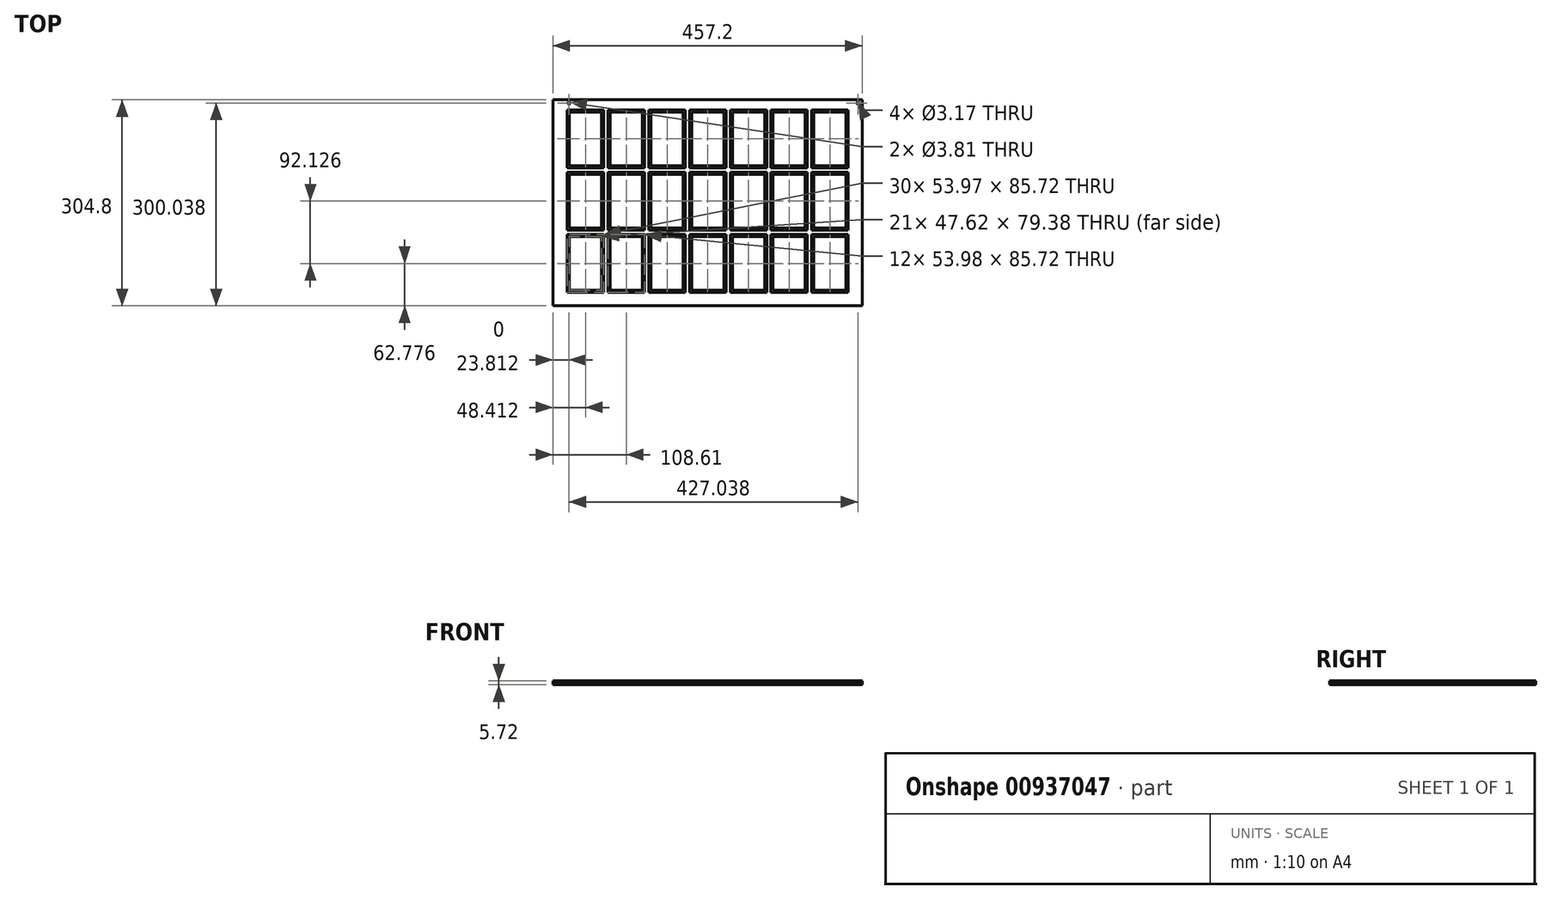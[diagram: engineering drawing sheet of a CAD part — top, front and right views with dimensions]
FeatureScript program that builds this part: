
annotation { "Feature Type Name" : "Feature", "Feature Type Description" : "" }
export const myFeature = defineFeature(function(context is Context, id is Id, definition is map)
    precondition{}
    {
        {
            var Q0;
            Q0=qCreatedBy(makeId("Top.planeOp"),FACE);
            var sketch = newSketch(context, id + "F0", { "sketchPlane" : qUnion([Q0])});
            skLineSegment(sketch, "E0.bottom", {"start": v(-228.6, 152.4) * mm, "end": v(228.6, 152.4) * mm});
            skLineSegment(sketch, "E0.top", {"start": v(-228.6, -152.4) * mm, "end": v(228.6, -152.4) * mm});
            skLineSegment(sketch, "E0.left", {"start": v(-228.6, 152.4) * mm, "end": v(-228.6, -152.4) * mm});
            skLineSegment(sketch, "E0.right", {"start": v(228.6, 152.4) * mm, "end": v(228.6, -152.4) * mm});
            skPoint(sketch, "E0.middle", {"position": v(0, 0) * mm});
            skCircle(sketch, "E1", {"center": v(-204.79, 147.64) * mm, "radius": 1.59 * mm});
            skCircle(sketch, "E2", {"center": v(222.25, 147.64) * mm, "radius": 1.59 * mm});
            skSolve(sketch);
        }
        {
            var Q0;
            Q0=makeQuery(id+"F0.imprint","IMPRINT",FACE,{"disambiguationData":[TD([[makeQuery(id+"F0.imprint","IMPRINT",EDGE,{"derivedFrom":sQuery(id+"F0.wireOp",EDGE,"E0.bottom")}),-1.0]])]});
            extrude(context, id + "F1", {"entities" : qUnion([Q0]), "depth" : 2.54 * mm, "offsetDistance" : 25.4 * mm});
        }
        {
            var Q0;
            Q0=makeQuery(id+"F1.opExtrude","CAP_FACE",FACE,{"disambiguationData":[OSD([sQuery(id+"F0.wireOp",EDGE,"E0.bottom"),sQuery(id+"F0.wireOp",EDGE,"E0.top"),sQuery(id+"F0.wireOp",EDGE,"E0.left"),sQuery(id+"F0.wireOp",EDGE,"E0.right"),sQuery(id+"F0.wireOp",EDGE,"E1"),sQuery(id+"F0.wireOp",EDGE,"E2")])],"isStart":false});
            var sketch = newSketch(context, id + "F2", { "sketchPlane" : qUnion([Q0])});
            skLineSegment(sketch, "E3.bottom", {"start": v(-207.18, -46.76) * mm, "end": v(-153.2, -46.76) * mm});
            skLineSegment(sketch, "E3.top", {"start": v(-207.18, -132.49) * mm, "end": v(-153.2, -132.49) * mm});
            skLineSegment(sketch, "E3.left", {"start": v(-207.18, -46.76) * mm, "end": v(-207.18, -132.49) * mm});
            skLineSegment(sketch, "E3.right", {"start": v(-153.2, -46.76) * mm, "end": v(-153.2, -132.49) * mm});
            skLineSegment(sketch, "E4.0.1.0", {"start": v(-207.18, 45.36) * mm, "end": v(-153.2, 45.36) * mm});
            skLineSegment(sketch, "E4.0.1.1", {"start": v(-207.18, 45.36) * mm, "end": v(-207.18, -40.36) * mm});
            skLineSegment(sketch, "E4.0.1.2", {"start": v(-207.18, -40.36) * mm, "end": v(-153.2, -40.36) * mm});
            skLineSegment(sketch, "E4.0.1.3", {"start": v(-153.2, 45.36) * mm, "end": v(-153.2, -40.36) * mm});
            skLineSegment(sketch, "E4.0.2.0", {"start": v(-207.18, 137.5) * mm, "end": v(-153.2, 137.5) * mm});
            skLineSegment(sketch, "E4.0.2.1", {"start": v(-207.18, 137.5) * mm, "end": v(-207.18, 51.77) * mm});
            skLineSegment(sketch, "E4.0.2.2", {"start": v(-207.18, 51.77) * mm, "end": v(-153.2, 51.77) * mm});
            skLineSegment(sketch, "E4.0.2.3", {"start": v(-153.2, 137.5) * mm, "end": v(-153.2, 51.77) * mm});
            skLineSegment(sketch, "E4.1.0.0", {"start": v(-146.98, -46.76) * mm, "end": v(-93, -46.76) * mm});
            skLineSegment(sketch, "E4.1.0.1", {"start": v(-146.98, -46.76) * mm, "end": v(-146.98, -132.49) * mm});
            skLineSegment(sketch, "E4.1.0.2", {"start": v(-146.98, -132.49) * mm, "end": v(-93, -132.49) * mm});
            skLineSegment(sketch, "E4.1.0.3", {"start": v(-93, -46.76) * mm, "end": v(-93, -132.49) * mm});
            skLineSegment(sketch, "E4.1.1.0", {"start": v(-146.98, 45.36) * mm, "end": v(-93, 45.36) * mm});
            skLineSegment(sketch, "E4.1.1.1", {"start": v(-146.98, 45.36) * mm, "end": v(-146.98, -40.36) * mm});
            skLineSegment(sketch, "E4.1.1.2", {"start": v(-146.98, -40.36) * mm, "end": v(-93, -40.36) * mm});
            skLineSegment(sketch, "E4.1.1.3", {"start": v(-93, 45.36) * mm, "end": v(-93, -40.36) * mm});
            skLineSegment(sketch, "E4.1.2.0", {"start": v(-146.98, 137.5) * mm, "end": v(-93, 137.5) * mm});
            skLineSegment(sketch, "E4.1.2.1", {"start": v(-146.98, 137.5) * mm, "end": v(-146.98, 51.77) * mm});
            skLineSegment(sketch, "E4.1.2.2", {"start": v(-146.98, 51.77) * mm, "end": v(-93, 51.77) * mm});
            skLineSegment(sketch, "E4.1.2.3", {"start": v(-93, 137.5) * mm, "end": v(-93, 51.77) * mm});
            skLineSegment(sketch, "E4.2.0.0", {"start": v(-86.78, -46.76) * mm, "end": v(-32.8, -46.76) * mm});
            skLineSegment(sketch, "E4.2.0.1", {"start": v(-86.78, -46.76) * mm, "end": v(-86.78, -132.49) * mm});
            skLineSegment(sketch, "E4.2.0.2", {"start": v(-86.78, -132.49) * mm, "end": v(-32.8, -132.49) * mm});
            skLineSegment(sketch, "E4.2.0.3", {"start": v(-32.8, -46.76) * mm, "end": v(-32.8, -132.49) * mm});
            skLineSegment(sketch, "E4.2.1.0", {"start": v(-86.78, 45.36) * mm, "end": v(-32.8, 45.36) * mm});
            skLineSegment(sketch, "E4.2.1.1", {"start": v(-86.78, 45.36) * mm, "end": v(-86.78, -40.36) * mm});
            skLineSegment(sketch, "E4.2.1.2", {"start": v(-86.78, -40.36) * mm, "end": v(-32.8, -40.36) * mm});
            skLineSegment(sketch, "E4.2.1.3", {"start": v(-32.8, 45.36) * mm, "end": v(-32.8, -40.36) * mm});
            skLineSegment(sketch, "E4.2.2.0", {"start": v(-86.78, 137.5) * mm, "end": v(-32.8, 137.5) * mm});
            skLineSegment(sketch, "E4.2.2.1", {"start": v(-86.78, 137.5) * mm, "end": v(-86.78, 51.77) * mm});
            skLineSegment(sketch, "E4.2.2.2", {"start": v(-86.78, 51.77) * mm, "end": v(-32.8, 51.77) * mm});
            skLineSegment(sketch, "E4.2.2.3", {"start": v(-32.8, 137.5) * mm, "end": v(-32.8, 51.77) * mm});
            skLineSegment(sketch, "E4.3.0.0", {"start": v(-26.58, -46.76) * mm, "end": v(27.4, -46.76) * mm});
            skLineSegment(sketch, "E4.3.0.1", {"start": v(-26.58, -46.76) * mm, "end": v(-26.58, -132.49) * mm});
            skLineSegment(sketch, "E4.3.0.2", {"start": v(-26.58, -132.49) * mm, "end": v(27.4, -132.49) * mm});
            skLineSegment(sketch, "E4.3.0.3", {"start": v(27.4, -46.76) * mm, "end": v(27.4, -132.49) * mm});
            skLineSegment(sketch, "E4.3.1.0", {"start": v(-26.58, 45.36) * mm, "end": v(27.4, 45.36) * mm});
            skLineSegment(sketch, "E4.3.1.1", {"start": v(-26.58, 45.36) * mm, "end": v(-26.58, -40.36) * mm});
            skLineSegment(sketch, "E4.3.1.2", {"start": v(-26.58, -40.36) * mm, "end": v(27.4, -40.36) * mm});
            skLineSegment(sketch, "E4.3.1.3", {"start": v(27.4, 45.36) * mm, "end": v(27.4, -40.36) * mm});
            skLineSegment(sketch, "E4.3.2.0", {"start": v(-26.58, 137.5) * mm, "end": v(27.4, 137.5) * mm});
            skLineSegment(sketch, "E4.3.2.1", {"start": v(-26.58, 137.5) * mm, "end": v(-26.58, 51.77) * mm});
            skLineSegment(sketch, "E4.3.2.2", {"start": v(-26.58, 51.77) * mm, "end": v(27.4, 51.77) * mm});
            skLineSegment(sketch, "E4.3.2.3", {"start": v(27.4, 137.5) * mm, "end": v(27.4, 51.77) * mm});
            skLineSegment(sketch, "E4.4.0.0", {"start": v(33.62, -46.76) * mm, "end": v(87.6, -46.76) * mm});
            skLineSegment(sketch, "E4.4.0.1", {"start": v(33.62, -46.76) * mm, "end": v(33.62, -132.49) * mm});
            skLineSegment(sketch, "E4.4.0.2", {"start": v(33.62, -132.49) * mm, "end": v(87.6, -132.49) * mm});
            skLineSegment(sketch, "E4.4.0.3", {"start": v(87.6, -46.76) * mm, "end": v(87.6, -132.49) * mm});
            skLineSegment(sketch, "E4.4.1.0", {"start": v(33.62, 45.36) * mm, "end": v(87.6, 45.36) * mm});
            skLineSegment(sketch, "E4.4.1.1", {"start": v(33.62, 45.36) * mm, "end": v(33.62, -40.36) * mm});
            skLineSegment(sketch, "E4.4.1.2", {"start": v(33.62, -40.36) * mm, "end": v(87.6, -40.36) * mm});
            skLineSegment(sketch, "E4.4.1.3", {"start": v(87.6, 45.36) * mm, "end": v(87.6, -40.36) * mm});
            skLineSegment(sketch, "E4.4.2.0", {"start": v(33.62, 137.5) * mm, "end": v(87.6, 137.5) * mm});
            skLineSegment(sketch, "E4.4.2.1", {"start": v(33.62, 137.5) * mm, "end": v(33.62, 51.77) * mm});
            skLineSegment(sketch, "E4.4.2.2", {"start": v(33.62, 51.77) * mm, "end": v(87.6, 51.77) * mm});
            skLineSegment(sketch, "E4.4.2.3", {"start": v(87.6, 137.5) * mm, "end": v(87.6, 51.77) * mm});
            skLineSegment(sketch, "E4.5.0.0", {"start": v(93.81, -46.76) * mm, "end": v(147.79, -46.76) * mm});
            skLineSegment(sketch, "E4.5.0.1", {"start": v(93.81, -46.76) * mm, "end": v(93.81, -132.49) * mm});
            skLineSegment(sketch, "E4.5.0.2", {"start": v(93.81, -132.49) * mm, "end": v(147.79, -132.49) * mm});
            skLineSegment(sketch, "E4.5.0.3", {"start": v(147.79, -46.76) * mm, "end": v(147.79, -132.49) * mm});
            skLineSegment(sketch, "E4.5.1.0", {"start": v(93.81, 45.36) * mm, "end": v(147.79, 45.36) * mm});
            skLineSegment(sketch, "E4.5.1.1", {"start": v(93.81, 45.36) * mm, "end": v(93.81, -40.36) * mm});
            skLineSegment(sketch, "E4.5.1.2", {"start": v(93.81, -40.36) * mm, "end": v(147.79, -40.36) * mm});
            skLineSegment(sketch, "E4.5.1.3", {"start": v(147.79, 45.36) * mm, "end": v(147.79, -40.36) * mm});
            skLineSegment(sketch, "E4.5.2.0", {"start": v(93.81, 137.5) * mm, "end": v(147.79, 137.5) * mm});
            skLineSegment(sketch, "E4.5.2.1", {"start": v(93.81, 137.5) * mm, "end": v(93.81, 51.77) * mm});
            skLineSegment(sketch, "E4.5.2.2", {"start": v(93.81, 51.77) * mm, "end": v(147.79, 51.77) * mm});
            skLineSegment(sketch, "E4.5.2.3", {"start": v(147.79, 137.5) * mm, "end": v(147.79, 51.77) * mm});
            skLineSegment(sketch, "E4.6.0.0", {"start": v(154.01, -46.76) * mm, "end": v(207.99, -46.76) * mm});
            skLineSegment(sketch, "E4.6.0.1", {"start": v(154.01, -46.76) * mm, "end": v(154.01, -132.49) * mm});
            skLineSegment(sketch, "E4.6.0.2", {"start": v(154.01, -132.49) * mm, "end": v(207.99, -132.49) * mm});
            skLineSegment(sketch, "E4.6.0.3", {"start": v(207.99, -46.76) * mm, "end": v(207.99, -132.49) * mm});
            skLineSegment(sketch, "E4.6.1.0", {"start": v(154.01, 45.36) * mm, "end": v(207.99, 45.36) * mm});
            skLineSegment(sketch, "E4.6.1.1", {"start": v(154.01, 45.36) * mm, "end": v(154.01, -40.36) * mm});
            skLineSegment(sketch, "E4.6.1.2", {"start": v(154.01, -40.36) * mm, "end": v(207.99, -40.36) * mm});
            skLineSegment(sketch, "E4.6.1.3", {"start": v(207.99, 45.36) * mm, "end": v(207.99, -40.36) * mm});
            skLineSegment(sketch, "E4.6.2.0", {"start": v(154.01, 137.5) * mm, "end": v(207.99, 137.5) * mm});
            skLineSegment(sketch, "E4.6.2.1", {"start": v(154.01, 137.5) * mm, "end": v(154.01, 51.77) * mm});
            skLineSegment(sketch, "E4.6.2.2", {"start": v(154.01, 51.77) * mm, "end": v(207.99, 51.77) * mm});
            skLineSegment(sketch, "E4.6.2.3", {"start": v(207.99, 137.5) * mm, "end": v(207.99, 51.77) * mm});
            skLineSegment(sketch, "E4.direction1", {"start": v(-207.18, -46.76) * mm, "end": v(-146.98, -46.76) * mm, "construction": true});
            skLineSegment(sketch, "E4.direction2", {"start": v(-207.18, -46.76) * mm, "end": v(-207.18, 45.36) * mm, "construction": true});
            skSolve(sketch);
        }
        {
            var Q0;
            Q0=makeQuery(id+"F2.imprint","IMPRINT",FACE,{"disambiguationData":[TD([[makeQuery(id+"F2.imprint","IMPRINT",EDGE,{"derivedFrom":sQuery(id+"F2.wireOp",EDGE,"E4.0.2.0")}),-1.0]])]});
            var Q1;
            Q1=makeQuery(id+"F2.imprint","IMPRINT",FACE,{"disambiguationData":[TD([[makeQuery(id+"F2.imprint","IMPRINT",EDGE,{"derivedFrom":sQuery(id+"F2.wireOp",EDGE,"E4.1.2.0")}),-1.0]])]});
            var Q2;
            Q2=makeQuery(id+"F2.imprint","IMPRINT",FACE,{"disambiguationData":[TD([[makeQuery(id+"F2.imprint","IMPRINT",EDGE,{"derivedFrom":sQuery(id+"F2.wireOp",EDGE,"E4.2.2.0")}),-1.0]])]});
            var Q3;
            Q3=makeQuery(id+"F2.imprint","IMPRINT",FACE,{"disambiguationData":[TD([[makeQuery(id+"F2.imprint","IMPRINT",EDGE,{"derivedFrom":sQuery(id+"F2.wireOp",EDGE,"E4.3.2.0")}),-1.0]])]});
            var Q4;
            Q4=makeQuery(id+"F2.imprint","IMPRINT",FACE,{"disambiguationData":[TD([[makeQuery(id+"F2.imprint","IMPRINT",EDGE,{"derivedFrom":sQuery(id+"F2.wireOp",EDGE,"E4.4.2.0")}),-1.0]])]});
            var Q5;
            Q5=makeQuery(id+"F2.imprint","IMPRINT",FACE,{"disambiguationData":[TD([[makeQuery(id+"F2.imprint","IMPRINT",EDGE,{"derivedFrom":sQuery(id+"F2.wireOp",EDGE,"E4.5.2.0")}),-1.0]])]});
            var Q6;
            Q6=makeQuery(id+"F2.imprint","IMPRINT",FACE,{"disambiguationData":[TD([[makeQuery(id+"F2.imprint","IMPRINT",EDGE,{"derivedFrom":sQuery(id+"F2.wireOp",EDGE,"E4.6.2.0")}),-1.0]])]});
            var Q7;
            Q7=makeQuery(id+"F2.imprint","IMPRINT",FACE,{"disambiguationData":[TD([[makeQuery(id+"F2.imprint","IMPRINT",EDGE,{"derivedFrom":sQuery(id+"F2.wireOp",EDGE,"E4.6.1.0")}),-1.0]])]});
            var Q8;
            Q8=makeQuery(id+"F2.imprint","IMPRINT",FACE,{"disambiguationData":[TD([[makeQuery(id+"F2.imprint","IMPRINT",EDGE,{"derivedFrom":sQuery(id+"F2.wireOp",EDGE,"E4.5.1.0")}),-1.0]])]});
            var Q9;
            Q9=makeQuery(id+"F2.imprint","IMPRINT",FACE,{"disambiguationData":[TD([[makeQuery(id+"F2.imprint","IMPRINT",EDGE,{"derivedFrom":sQuery(id+"F2.wireOp",EDGE,"E4.4.1.0")}),-1.0]])]});
            var Q10;
            Q10=makeQuery(id+"F2.imprint","IMPRINT",FACE,{"disambiguationData":[TD([[makeQuery(id+"F2.imprint","IMPRINT",EDGE,{"derivedFrom":sQuery(id+"F2.wireOp",EDGE,"E4.3.1.0")}),-1.0]])]});
            var Q11;
            Q11=makeQuery(id+"F2.imprint","IMPRINT",FACE,{"disambiguationData":[TD([[makeQuery(id+"F2.imprint","IMPRINT",EDGE,{"derivedFrom":sQuery(id+"F2.wireOp",EDGE,"E4.2.1.0")}),-1.0]])]});
            var Q12;
            Q12=makeQuery(id+"F2.imprint","IMPRINT",FACE,{"disambiguationData":[TD([[makeQuery(id+"F2.imprint","IMPRINT",EDGE,{"derivedFrom":sQuery(id+"F2.wireOp",EDGE,"E4.1.1.0")}),-1.0]])]});
            var Q13;
            Q13=makeQuery(id+"F2.imprint","IMPRINT",FACE,{"disambiguationData":[TD([[makeQuery(id+"F2.imprint","IMPRINT",EDGE,{"derivedFrom":sQuery(id+"F2.wireOp",EDGE,"E4.0.1.0")}),-1.0]])]});
            var Q14;
            Q14=makeQuery(id+"F2.imprint","IMPRINT",FACE,{"disambiguationData":[TD([[makeQuery(id+"F2.imprint","IMPRINT",EDGE,{"derivedFrom":sQuery(id+"F2.wireOp",EDGE,"E3.bottom")}),-1.0]])]});
            var Q15;
            Q15=makeQuery(id+"F2.imprint","IMPRINT",FACE,{"disambiguationData":[TD([[makeQuery(id+"F2.imprint","IMPRINT",EDGE,{"derivedFrom":sQuery(id+"F2.wireOp",EDGE,"E4.1.0.0")}),-1.0]])]});
            var Q16;
            Q16=makeQuery(id+"F2.imprint","IMPRINT",FACE,{"disambiguationData":[TD([[makeQuery(id+"F2.imprint","IMPRINT",EDGE,{"derivedFrom":sQuery(id+"F2.wireOp",EDGE,"E4.2.0.0")}),-1.0]])]});
            var Q17;
            Q17=makeQuery(id+"F2.imprint","IMPRINT",FACE,{"disambiguationData":[TD([[makeQuery(id+"F2.imprint","IMPRINT",EDGE,{"derivedFrom":sQuery(id+"F2.wireOp",EDGE,"E4.3.0.0")}),-1.0]])]});
            var Q18;
            Q18=makeQuery(id+"F2.imprint","IMPRINT",FACE,{"disambiguationData":[TD([[makeQuery(id+"F2.imprint","IMPRINT",EDGE,{"derivedFrom":sQuery(id+"F2.wireOp",EDGE,"E4.4.0.0")}),-1.0]])]});
            var Q19;
            Q19=makeQuery(id+"F2.imprint","IMPRINT",FACE,{"disambiguationData":[TD([[makeQuery(id+"F2.imprint","IMPRINT",EDGE,{"derivedFrom":sQuery(id+"F2.wireOp",EDGE,"E4.5.0.0")}),-1.0]])]});
            var Q20;
            Q20=makeQuery(id+"F2.imprint","IMPRINT",FACE,{"disambiguationData":[TD([[makeQuery(id+"F2.imprint","IMPRINT",EDGE,{"derivedFrom":sQuery(id+"F2.wireOp",EDGE,"E4.6.0.0")}),-1.0]])]});
            extrude(context, id + "F3", {"entities" : qUnion([Q0, Q1, Q2, Q3, Q4, Q5, Q6, Q7, Q8, Q9, Q10, Q11, Q12, Q13, Q14, Q15, Q16, Q17, Q18, Q19, Q20]), "operationType" : NewBodyOperationType.REMOVE, "oppositeDirection" : true, "depth" : 25.4 * mm, "offsetDistance" : 25.4 * mm});
        }
        {
            var Q0;
            Q0=qCreatedBy(makeId("Top.planeOp"),FACE);
            var sketch = newSketch(context, id + "F4", { "sketchPlane" : qUnion([Q0])});
            skLineSegment(sketch, "E5.0.0", {"start": v(-228.6, 152.4) * mm, "end": v(-228.6, -152.4) * mm});
            skLineSegment(sketch, "E5.0.1", {"start": v(-228.6, -152.4) * mm, "end": v(228.6, -152.4) * mm});
            skLineSegment(sketch, "E5.0.2", {"start": v(228.6, -152.4) * mm, "end": v(228.6, 152.4) * mm});
            skLineSegment(sketch, "E5.0.3", {"start": v(228.6, 152.4) * mm, "end": v(-228.6, 152.4) * mm});
            skLineSegment(sketch, "E6.bottom", {"start": v(-204, 134.32) * mm, "end": v(-156.38, 134.32) * mm});
            skLineSegment(sketch, "E6.top", {"start": v(-204, 54.94) * mm, "end": v(-156.38, 54.94) * mm});
            skLineSegment(sketch, "E6.left", {"start": v(-204, 134.32) * mm, "end": v(-204, 54.94) * mm});
            skLineSegment(sketch, "E6.right", {"start": v(-156.38, 134.32) * mm, "end": v(-156.38, 54.94) * mm});
            skPoint(sketch, "E7.0", {"position": v(-207.18, 137.5) * mm});
            skPoint(sketch, "E8.0", {"position": v(-146.98, 137.5) * mm});
            skPoint(sketch, "E9.0", {"position": v(-207.18, 45.36) * mm});
            skLineSegment(sketch, "E10.0.1.0", {"start": v(-204, 42.19) * mm, "end": v(-156.38, 42.19) * mm});
            skLineSegment(sketch, "E10.0.1.1", {"start": v(-204, 42.19) * mm, "end": v(-204, -37.19) * mm});
            skLineSegment(sketch, "E10.0.1.2", {"start": v(-204, -37.19) * mm, "end": v(-156.38, -37.19) * mm});
            skLineSegment(sketch, "E10.0.1.3", {"start": v(-156.38, 42.19) * mm, "end": v(-156.38, -37.19) * mm});
            skLineSegment(sketch, "E10.0.2.0", {"start": v(-204, -49.94) * mm, "end": v(-156.38, -49.94) * mm});
            skLineSegment(sketch, "E10.0.2.1", {"start": v(-204, -49.94) * mm, "end": v(-204, -129.31) * mm});
            skLineSegment(sketch, "E10.0.2.2", {"start": v(-204, -129.31) * mm, "end": v(-156.38, -129.31) * mm});
            skLineSegment(sketch, "E10.0.2.3", {"start": v(-156.38, -49.94) * mm, "end": v(-156.38, -129.31) * mm});
            skLineSegment(sketch, "E10.1.0.0", {"start": v(-143.8, 134.32) * mm, "end": v(-96.18, 134.32) * mm});
            skLineSegment(sketch, "E10.1.0.1", {"start": v(-143.8, 134.32) * mm, "end": v(-143.8, 54.94) * mm});
            skLineSegment(sketch, "E10.1.0.2", {"start": v(-143.8, 54.94) * mm, "end": v(-96.18, 54.94) * mm});
            skLineSegment(sketch, "E10.1.0.3", {"start": v(-96.18, 134.32) * mm, "end": v(-96.18, 54.94) * mm});
            skLineSegment(sketch, "E10.1.1.0", {"start": v(-143.8, 42.19) * mm, "end": v(-96.18, 42.19) * mm});
            skLineSegment(sketch, "E10.1.1.1", {"start": v(-143.8, 42.19) * mm, "end": v(-143.8, -37.19) * mm});
            skLineSegment(sketch, "E10.1.1.2", {"start": v(-143.8, -37.19) * mm, "end": v(-96.18, -37.19) * mm});
            skLineSegment(sketch, "E10.1.1.3", {"start": v(-96.18, 42.19) * mm, "end": v(-96.18, -37.19) * mm});
            skLineSegment(sketch, "E10.1.2.0", {"start": v(-143.8, -49.94) * mm, "end": v(-96.18, -49.94) * mm});
            skLineSegment(sketch, "E10.1.2.1", {"start": v(-143.8, -49.94) * mm, "end": v(-143.8, -129.31) * mm});
            skLineSegment(sketch, "E10.1.2.2", {"start": v(-143.8, -129.31) * mm, "end": v(-96.18, -129.31) * mm});
            skLineSegment(sketch, "E10.1.2.3", {"start": v(-96.18, -49.94) * mm, "end": v(-96.18, -129.31) * mm});
            skLineSegment(sketch, "E10.2.0.0", {"start": v(-83.6, 134.32) * mm, "end": v(-35.98, 134.32) * mm});
            skLineSegment(sketch, "E10.2.0.1", {"start": v(-83.6, 134.32) * mm, "end": v(-83.6, 54.94) * mm});
            skLineSegment(sketch, "E10.2.0.2", {"start": v(-83.6, 54.94) * mm, "end": v(-35.98, 54.94) * mm});
            skLineSegment(sketch, "E10.2.0.3", {"start": v(-35.98, 134.32) * mm, "end": v(-35.98, 54.94) * mm});
            skLineSegment(sketch, "E10.2.1.0", {"start": v(-83.6, 42.19) * mm, "end": v(-35.98, 42.19) * mm});
            skLineSegment(sketch, "E10.2.1.1", {"start": v(-83.6, 42.19) * mm, "end": v(-83.6, -37.19) * mm});
            skLineSegment(sketch, "E10.2.1.2", {"start": v(-83.6, -37.19) * mm, "end": v(-35.98, -37.19) * mm});
            skLineSegment(sketch, "E10.2.1.3", {"start": v(-35.98, 42.19) * mm, "end": v(-35.98, -37.19) * mm});
            skLineSegment(sketch, "E10.2.2.0", {"start": v(-83.6, -49.94) * mm, "end": v(-35.98, -49.94) * mm});
            skLineSegment(sketch, "E10.2.2.1", {"start": v(-83.6, -49.94) * mm, "end": v(-83.6, -129.31) * mm});
            skLineSegment(sketch, "E10.2.2.2", {"start": v(-83.6, -129.31) * mm, "end": v(-35.98, -129.31) * mm});
            skLineSegment(sketch, "E10.2.2.3", {"start": v(-35.98, -49.94) * mm, "end": v(-35.98, -129.31) * mm});
            skLineSegment(sketch, "E10.3.0.0", {"start": v(-23.4, 134.32) * mm, "end": v(24.22, 134.32) * mm});
            skLineSegment(sketch, "E10.3.0.1", {"start": v(-23.4, 134.32) * mm, "end": v(-23.4, 54.94) * mm});
            skLineSegment(sketch, "E10.3.0.2", {"start": v(-23.4, 54.94) * mm, "end": v(24.22, 54.94) * mm});
            skLineSegment(sketch, "E10.3.0.3", {"start": v(24.22, 134.32) * mm, "end": v(24.22, 54.94) * mm});
            skLineSegment(sketch, "E10.3.1.0", {"start": v(-23.4, 42.19) * mm, "end": v(24.22, 42.19) * mm});
            skLineSegment(sketch, "E10.3.1.1", {"start": v(-23.4, 42.19) * mm, "end": v(-23.4, -37.19) * mm});
            skLineSegment(sketch, "E10.3.1.2", {"start": v(-23.4, -37.19) * mm, "end": v(24.22, -37.19) * mm});
            skLineSegment(sketch, "E10.3.1.3", {"start": v(24.22, 42.19) * mm, "end": v(24.22, -37.19) * mm});
            skLineSegment(sketch, "E10.3.2.0", {"start": v(-23.4, -49.94) * mm, "end": v(24.22, -49.94) * mm});
            skLineSegment(sketch, "E10.3.2.1", {"start": v(-23.4, -49.94) * mm, "end": v(-23.4, -129.31) * mm});
            skLineSegment(sketch, "E10.3.2.2", {"start": v(-23.4, -129.31) * mm, "end": v(24.22, -129.31) * mm});
            skLineSegment(sketch, "E10.3.2.3", {"start": v(24.22, -49.94) * mm, "end": v(24.22, -129.31) * mm});
            skLineSegment(sketch, "E10.4.0.0", {"start": v(36.8, 134.32) * mm, "end": v(84.42, 134.32) * mm});
            skLineSegment(sketch, "E10.4.0.1", {"start": v(36.8, 134.32) * mm, "end": v(36.8, 54.94) * mm});
            skLineSegment(sketch, "E10.4.0.2", {"start": v(36.8, 54.94) * mm, "end": v(84.42, 54.94) * mm});
            skLineSegment(sketch, "E10.4.0.3", {"start": v(84.42, 134.32) * mm, "end": v(84.42, 54.94) * mm});
            skLineSegment(sketch, "E10.4.1.0", {"start": v(36.8, 42.19) * mm, "end": v(84.42, 42.19) * mm});
            skLineSegment(sketch, "E10.4.1.1", {"start": v(36.8, 42.19) * mm, "end": v(36.8, -37.19) * mm});
            skLineSegment(sketch, "E10.4.1.2", {"start": v(36.8, -37.19) * mm, "end": v(84.42, -37.19) * mm});
            skLineSegment(sketch, "E10.4.1.3", {"start": v(84.42, 42.19) * mm, "end": v(84.42, -37.19) * mm});
            skLineSegment(sketch, "E10.4.2.0", {"start": v(36.8, -49.94) * mm, "end": v(84.42, -49.94) * mm});
            skLineSegment(sketch, "E10.4.2.1", {"start": v(36.8, -49.94) * mm, "end": v(36.8, -129.31) * mm});
            skLineSegment(sketch, "E10.4.2.2", {"start": v(36.8, -129.31) * mm, "end": v(84.42, -129.31) * mm});
            skLineSegment(sketch, "E10.4.2.3", {"start": v(84.42, -49.94) * mm, "end": v(84.42, -129.31) * mm});
            skLineSegment(sketch, "E10.5.0.0", {"start": v(96.99, 134.32) * mm, "end": v(144.61, 134.32) * mm});
            skLineSegment(sketch, "E10.5.0.1", {"start": v(96.99, 134.32) * mm, "end": v(96.99, 54.94) * mm});
            skLineSegment(sketch, "E10.5.0.2", {"start": v(96.99, 54.94) * mm, "end": v(144.61, 54.94) * mm});
            skLineSegment(sketch, "E10.5.0.3", {"start": v(144.61, 134.32) * mm, "end": v(144.61, 54.94) * mm});
            skLineSegment(sketch, "E10.5.1.0", {"start": v(96.99, 42.19) * mm, "end": v(144.61, 42.19) * mm});
            skLineSegment(sketch, "E10.5.1.1", {"start": v(96.99, 42.19) * mm, "end": v(96.99, -37.19) * mm});
            skLineSegment(sketch, "E10.5.1.2", {"start": v(96.99, -37.19) * mm, "end": v(144.61, -37.19) * mm});
            skLineSegment(sketch, "E10.5.1.3", {"start": v(144.61, 42.19) * mm, "end": v(144.61, -37.19) * mm});
            skLineSegment(sketch, "E10.5.2.0", {"start": v(96.99, -49.94) * mm, "end": v(144.61, -49.94) * mm});
            skLineSegment(sketch, "E10.5.2.1", {"start": v(96.99, -49.94) * mm, "end": v(96.99, -129.31) * mm});
            skLineSegment(sketch, "E10.5.2.2", {"start": v(96.99, -129.31) * mm, "end": v(144.61, -129.31) * mm});
            skLineSegment(sketch, "E10.5.2.3", {"start": v(144.61, -49.94) * mm, "end": v(144.61, -129.31) * mm});
            skLineSegment(sketch, "E10.6.0.0", {"start": v(157.19, 134.32) * mm, "end": v(204.81, 134.32) * mm});
            skLineSegment(sketch, "E10.6.0.1", {"start": v(157.19, 134.32) * mm, "end": v(157.19, 54.94) * mm});
            skLineSegment(sketch, "E10.6.0.2", {"start": v(157.19, 54.94) * mm, "end": v(204.81, 54.94) * mm});
            skLineSegment(sketch, "E10.6.0.3", {"start": v(204.81, 134.32) * mm, "end": v(204.81, 54.94) * mm});
            skLineSegment(sketch, "E10.6.1.0", {"start": v(157.19, 42.19) * mm, "end": v(204.81, 42.19) * mm});
            skLineSegment(sketch, "E10.6.1.1", {"start": v(157.19, 42.19) * mm, "end": v(157.19, -37.19) * mm});
            skLineSegment(sketch, "E10.6.1.2", {"start": v(157.19, -37.19) * mm, "end": v(204.81, -37.19) * mm});
            skLineSegment(sketch, "E10.6.1.3", {"start": v(204.81, 42.19) * mm, "end": v(204.81, -37.19) * mm});
            skLineSegment(sketch, "E10.6.2.0", {"start": v(157.19, -49.94) * mm, "end": v(204.81, -49.94) * mm});
            skLineSegment(sketch, "E10.6.2.1", {"start": v(157.19, -49.94) * mm, "end": v(157.19, -129.31) * mm});
            skLineSegment(sketch, "E10.6.2.2", {"start": v(157.19, -129.31) * mm, "end": v(204.81, -129.31) * mm});
            skLineSegment(sketch, "E10.6.2.3", {"start": v(204.81, -49.94) * mm, "end": v(204.81, -129.31) * mm});
            skLineSegment(sketch, "E10.direction1", {"start": v(-204, 134.32) * mm, "end": v(-143.8, 134.32) * mm, "construction": true});
            skLineSegment(sketch, "E10.direction2", {"start": v(-204, 134.32) * mm, "end": v(-204, 42.19) * mm, "construction": true});
            skCircle(sketch, "E11.0", {"center": v(-204.79, 147.64) * mm, "radius": 1.59 * mm});
            skCircle(sketch, "E12.0", {"center": v(222.25, 147.64) * mm, "radius": 1.59 * mm});
            skCircle(sketch, "E13", {"center": v(222.25, 147.64) * mm, "radius": 1.9 * mm});
            skCircle(sketch, "E14", {"center": v(-204.79, 147.64) * mm, "radius": 1.9 * mm});
            skSolve(sketch);
        }
        {
            var Q0;
            Q0=makeQuery(id+"F1.opExtrude","CAP_FACE",FACE,{"disambiguationData":[OSD([sQuery(id+"F0.wireOp",EDGE,"E0.bottom"),sQuery(id+"F0.wireOp",EDGE,"E0.top"),sQuery(id+"F0.wireOp",EDGE,"E0.left"),sQuery(id+"F0.wireOp",EDGE,"E0.right"),sQuery(id+"F0.wireOp",EDGE,"E1"),sQuery(id+"F0.wireOp",EDGE,"E2")])],"isStart":false});
            var Q1;
            Q1=makeQuery(id+"F4.imprint","IMPRINT",FACE,{"disambiguationData":[TD([[makeQuery(id+"F4.imprint","IMPRINT",EDGE,{"derivedFrom":sQuery(id+"F4.wireOp",EDGE,"E5.0.0")}),1.0]])]});
            extrude(context, id + "F5", {"entities" : qUnion([Q0, Q1]), "oppositeDirection" : true, "depth" : 3.17 * mm, "offsetDistance" : 25.4 * mm});
        }
    });
